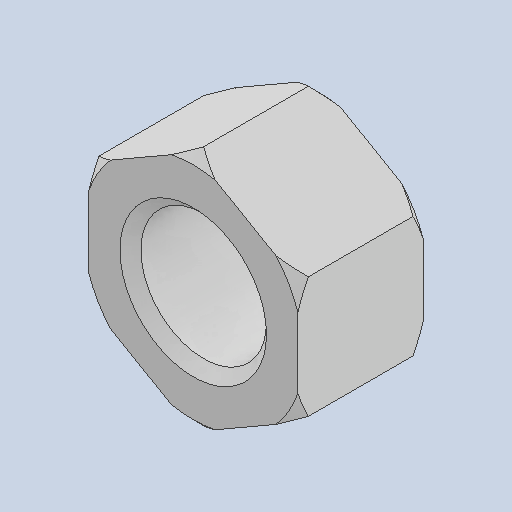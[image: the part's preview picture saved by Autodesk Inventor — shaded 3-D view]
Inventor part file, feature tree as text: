
AUTODESK INVENTOR PART (.ipt)
format: ipt  version: 2022 (Build 260153000, 153)  size: 133,632 bytes
history: native  units: in
note: dims shown in document units (in); Inventor stores cm internally (conversion verified against a paired STEP export)
features: chamfer x1
ambient origin geometry x8: Origin, YZ Plane, XZ Plane, XY Plane, X Axis, Y Axis, Z Axis, Center Point
bodies: Solid1 (feature_tree)
feature tree (1):
  chamfer  "Chamfer2"  [1 undecoded]
note: 1 required parameter value undecoded (feature->parameter linkage not recoverable at this tier; creation-order binding heuristic only, values carry confidence <= 0.55)
